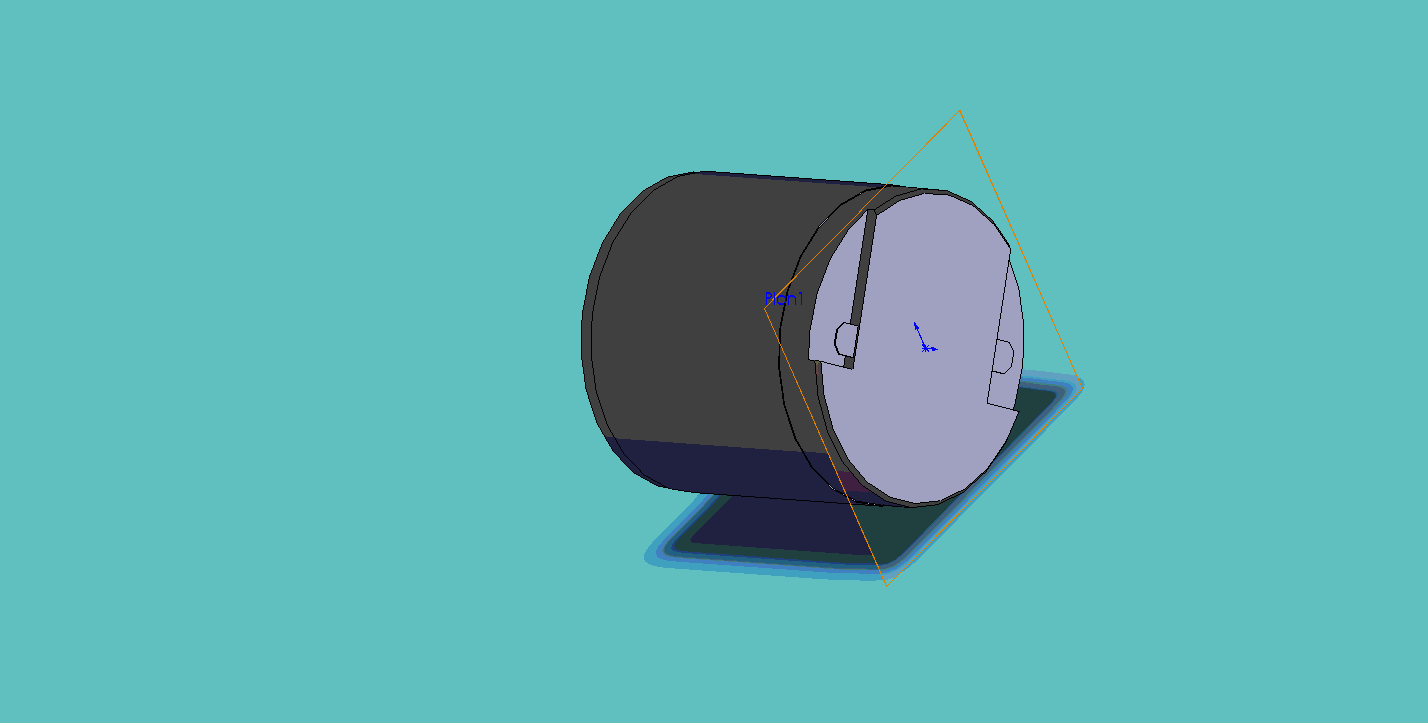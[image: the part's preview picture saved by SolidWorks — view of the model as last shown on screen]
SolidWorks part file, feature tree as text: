
SOLIDWORKS PART (.sldprt)
format: sldprt  version: not decoded by parser v0  size: 198,656 bytes
history: native  units: mm
features: plane x4, chamfer x4, sketch x3, material x1, revolve x1, cut_extrude x1, extrude x1 (+12 scaffold rows collapsed)
feature tree (27):
  scaffold x12  (default folders/planes/origin — collapsed)
  material  "Matériau <non spécifié>"
  plane  "Plan de face"
  plane  "Plan de dessus"
  plane  "Plan de droite"
  sketch  "Esquisse1"  dims[D1=30.0mm D2=29.8mm D3=29.7mm D4=30.0mm D5=4.9mm D6=1.4mm D7=8.0mm D8=2.0mm D9=8.2mm D10=4.2mm D11=2.0mm D12=1.1mm]
  revolve  "Révolution1"  Angle=360deg
  sketch  "Esquisse2"  dims[c1.D1=~20.492854mm c2.D1=45.0deg c2.D2=19.0mm c2.D3=3.6mm]
  cut_extrude  "Enlèv. mat.-Extru.2"  Depth=1.2mm
  chamfer  "Chanfrein1"  Distance=0.2mm Angle=45deg
  plane  "Plan1"  Offset=0.3mm
  sketch  "Esquisse3"  dims[D1=3.0mm D2=2.75mm D3=0.5mm D4=0.5mm]
  extrude  "Extrusion1"  Depth=0.13mm
  chamfer  "Chanfrein2"  Distance=0.8mm Angle=45deg
  chamfer  "Chanfrein3"  Distance=0.4mm Angle=45deg
  chamfer  "Chanfrein4"  Distance=0.2mm Angle=30deg
decode coverage: 10 of 10 modeling features carry decoded parameters
note: ~ marks probable driven/reference dimensions
note: suppression state not decoded; provenance and decode notes live in map.json
